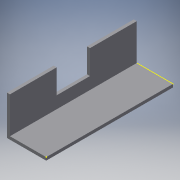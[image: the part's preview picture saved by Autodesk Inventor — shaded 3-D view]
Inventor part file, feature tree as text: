
AUTODESK INVENTOR PART (.ipt)
format: ipt  version: 2017 (Build 210142000, 142)  size: 124,416 bytes
history: native  units: in
note: dims shown in document units (in); Inventor stores cm internally (conversion verified against a paired STEP export)
features: sketch x5, extrude x4
ambient origin geometry x8: Origin, YZ Plane, XZ Plane, XY Plane, X Axis, Y Axis, Z Axis, Center Point
bodies: Solid1 (feature_tree)
feature tree (9):
  extrude  "Extrusion1"  Depth=1.625in
  extrude  "Extrusion2"  Depth=0.125in
  extrude  "Extrusion3"  Depth=1.5in
  sketch  "Sketch4"  dims[d8=0.688in d9=1.0in d10=0.0in]
  extrude  "Extrusion4"  Depth=1.0in TaperAngle=0.0deg
  sketch  "Sketch1"  dims[d0=5.25in d1=1.625in]
  sketch  "Sketch2"  dims[d2=0.125in d3=0.0in d4=0.125in]
  sketch  "Sketch3"  dims[d5=1.5in d6=0.0in d7=0.6875in]
  sketch  "Sketch5"  dims[d12=2.024in d13=2.024in d14=0.15in d15=0.15in d16=0.8125in d17=0.0in]
